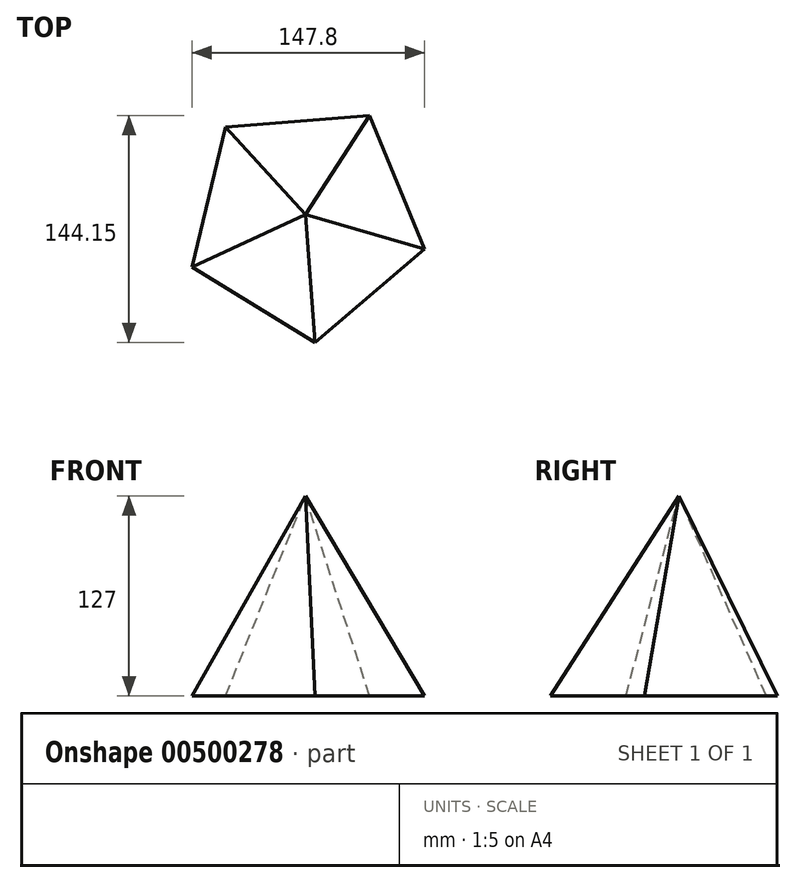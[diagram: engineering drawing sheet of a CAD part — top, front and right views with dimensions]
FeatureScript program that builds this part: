
annotation { "Feature Type Name" : "Feature", "Feature Type Description" : "" }
export const myFeature = defineFeature(function(context is Context, id is Id, definition is map)
    precondition{}
    {
        {
            var Q0;
            Q0=qCreatedBy(makeId("Top.planeOp"),FACE);
            var sketch = newSketch(context, id + "F0", { "sketchPlane" : qUnion([Q0])});
            skCircle(sketch, "E0.cCircle", {"center": v(0, 0) * mm, "radius": 77.94 * mm, "construction": true});
            skLineSegment(sketch, "E0.0", {"start": v(75.78, -18.22) * mm, "end": v(6.1, -77.7) * mm});
            skLineSegment(sketch, "E0.1", {"start": v(6.1, -77.7) * mm, "end": v(-72.02, -29.8) * mm});
            skLineSegment(sketch, "E0.2", {"start": v(-72.02, -29.8) * mm, "end": v(-50.6, 59.28) * mm});
            skLineSegment(sketch, "E0.3", {"start": v(-50.6, 59.28) * mm, "end": v(40.74, 66.45) * mm});
            skLineSegment(sketch, "E0.4", {"start": v(40.74, 66.45) * mm, "end": v(75.78, -18.22) * mm});
            skSolve(sketch);
        }
        {
            var Q0;
            Q0=qCreatedBy(makeId("Top.planeOp"),FACE);
            cPlane(context, id + "F1", {"entities" : qUnion([Q0]), "cplaneType" : CPlaneType.OFFSET, "offset" : 127 * mm, "width" : 152.4 * mm, "height" : 152.4 * mm});
        }
        {
            var Q0;
            Q0=qCreatedBy(id+"F1.planeOp",FACE);
            var sketch = newSketch(context, id + "F2", { "sketchPlane" : qUnion([Q0])});
            skPoint(sketch, "E1", {"position": v(0, 3.71) * mm});
            skSolve(sketch);
        }
        {
            var Q0;
            Q0=makeQuery(id+"F0.imprint","IMPRINT",FACE,{"disambiguationData":[TD([[makeQuery(id+"F0.imprint","IMPRINT",EDGE,{"derivedFrom":sQuery(id+"F0.wireOp",EDGE,"E0.0")}),-1.0]])]});
            var Q1;
            Q1=sQuery(id+"F2.wireOp",VERTEX,"E1");
            loft(context, id + "F3", {"sheetProfilesArray" : [{ "sheetProfileEntities" : qUnion([Q0]) }, { "sheetProfileEntities" : qUnion([Q1]) }]});
        }
    });
